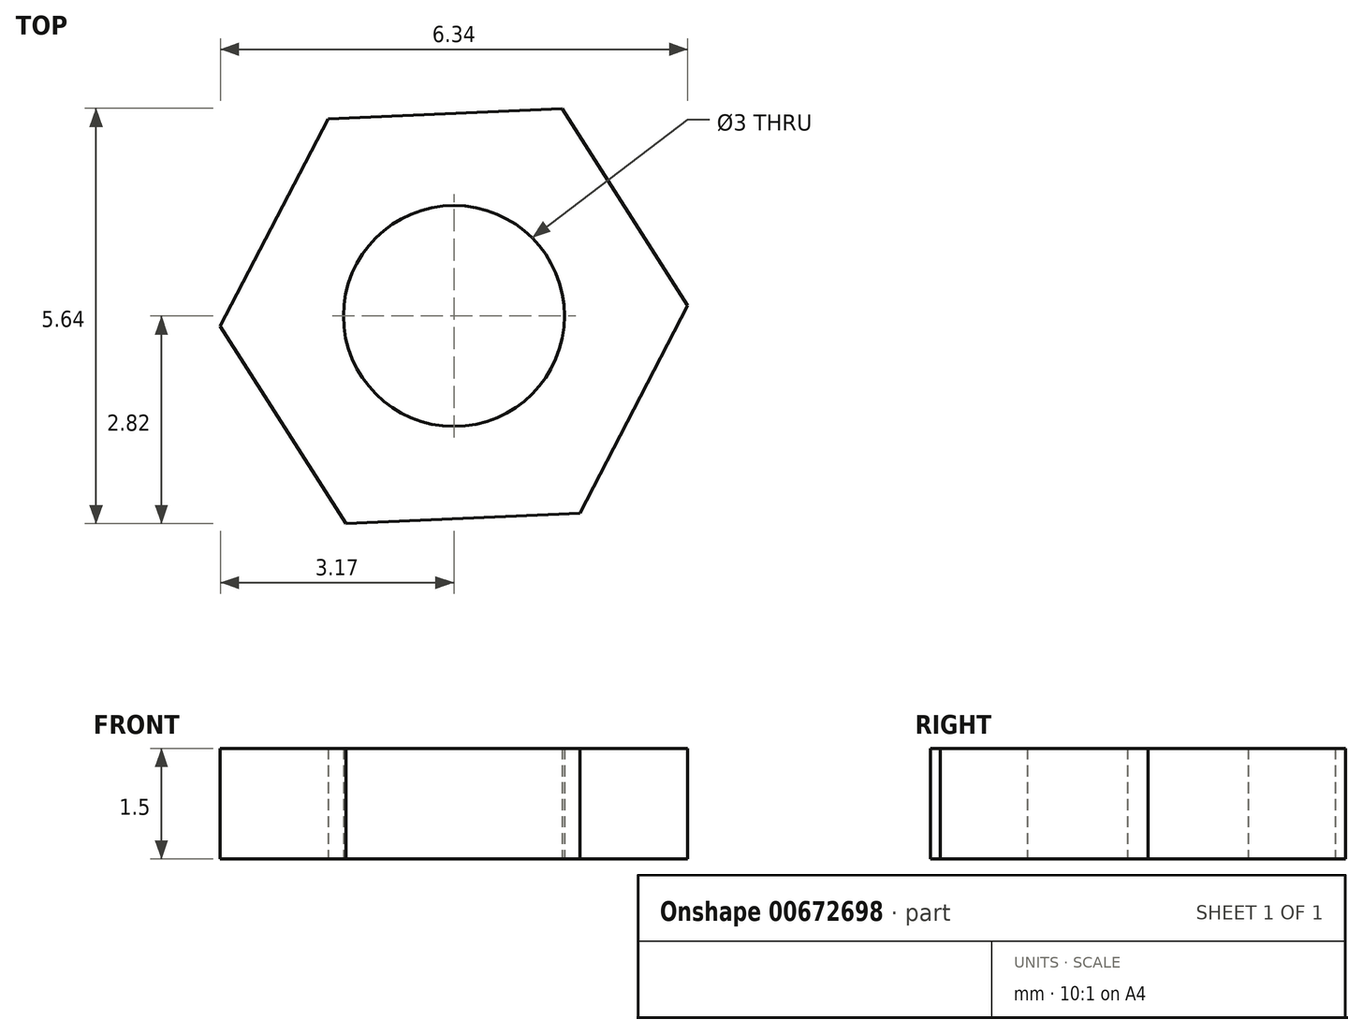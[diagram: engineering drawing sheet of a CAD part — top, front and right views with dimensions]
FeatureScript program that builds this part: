
annotation { "Feature Type Name" : "Feature", "Feature Type Description" : "" }
export const myFeature = defineFeature(function(context is Context, id is Id, definition is map)
    precondition{}
    {
        {
            var Q0;
            Q0=qCreatedBy(makeId("Top.planeOp"),FACE);
            var sketch = newSketch(context, id + "F0", { "sketchPlane" : qUnion([Q0])});
            skCircle(sketch, "E0.cCircle", {"center": v(0, 0) * mm, "radius": 2.75 * mm});
            skLineSegment(sketch, "E0.0", {"start": v(3.17, 0.14) * mm, "end": v(1.7, -2.68) * mm});
            skLineSegment(sketch, "E0.1", {"start": v(1.7, -2.68) * mm, "end": v(-1.47, -2.82) * mm});
            skLineSegment(sketch, "E0.2", {"start": v(-1.47, -2.82) * mm, "end": v(-3.17, -0.14) * mm});
            skLineSegment(sketch, "E0.3", {"start": v(-3.17, -0.14) * mm, "end": v(-1.7, 2.68) * mm});
            skLineSegment(sketch, "E0.4", {"start": v(-1.7, 2.68) * mm, "end": v(1.47, 2.82) * mm});
            skLineSegment(sketch, "E0.5", {"start": v(1.47, 2.82) * mm, "end": v(3.17, 0.14) * mm});
            skPoint(sketch, "E0.0.midPoint", {"position": v(2.44, -1.27) * mm});
            skCircle(sketch, "E1", {"center": v(0, 0) * mm, "radius": 1.5 * mm});
            skPoint(sketch, "E2", {"position": v(-1.47, -2.82) * mm});
            skPoint(sketch, "E3", {"position": v(1.7, -2.68) * mm});
            skSolve(sketch);
        }
        {
            var Q0;
            {var subQ0=sQuery(id+"F0.wireOp",EDGE,"E0.4");var subQ1=sQuery(id+"F0.wireOp",EDGE,"E0.cCircle");var subQ2=makeQuery(id+"F0.imprint","INTERSECT",VERTEX,{"derivedFrom":[subQ1,subQ0]});Q0=makeQuery(id+"F0.imprint","IMPRINT",FACE,{"disambiguationData":[TD([[makeQuery(id+"F0.imprint","IMPRINT",EDGE,{"disambiguationData":[TD([[subQ2,1.0]])],"derivedFrom":subQ1}),-1.0]])]});}
            var Q1;
            {var subQ0=sQuery(id+"F0.wireOp",EDGE,"E0.1");var subQ1=sQuery(id+"F0.wireOp",EDGE,"E0.cCircle");var subQ2=makeQuery(id+"F0.imprint","INTERSECT",VERTEX,{"derivedFrom":[subQ1,subQ0]});Q1=makeQuery(id+"F0.imprint","IMPRINT",FACE,{"disambiguationData":[TD([[makeQuery(id+"F0.imprint","IMPRINT",EDGE,{"disambiguationData":[TD([[subQ2,-1.0]])],"derivedFrom":subQ1}),-1.0]])]});}
            var Q2;
            {var subQ0=sQuery(id+"F0.wireOp",EDGE,"E0.4");var subQ1=sQuery(id+"F0.wireOp",EDGE,"E0.cCircle");var subQ2=makeQuery(id+"F0.imprint","INTERSECT",VERTEX,{"derivedFrom":[subQ1,subQ0]});Q2=makeQuery(id+"F0.imprint","IMPRINT",FACE,{"disambiguationData":[TD([[makeQuery(id+"F0.imprint","IMPRINT",EDGE,{"disambiguationData":[TD([[subQ2,-1.0]])],"derivedFrom":subQ1}),-1.0]])]});}
            var Q3;
            {var subQ0=sQuery(id+"F0.wireOp",EDGE,"E0.5");var subQ1=sQuery(id+"F0.wireOp",EDGE,"E0.cCircle");var subQ2=makeQuery(id+"F0.imprint","INTERSECT",VERTEX,{"derivedFrom":[subQ1,subQ0]});Q3=makeQuery(id+"F0.imprint","IMPRINT",FACE,{"disambiguationData":[TD([[makeQuery(id+"F0.imprint","IMPRINT",EDGE,{"disambiguationData":[TD([[subQ2,1.0]])],"derivedFrom":subQ1}),-1.0]])]});}
            var Q4;
            {var subQ0=sQuery(id+"F0.wireOp",EDGE,"E0.2");var subQ1=sQuery(id+"F0.wireOp",EDGE,"E0.cCircle");var subQ2=makeQuery(id+"F0.imprint","INTERSECT",VERTEX,{"derivedFrom":[subQ1,subQ0]});Q4=makeQuery(id+"F0.imprint","IMPRINT",FACE,{"disambiguationData":[TD([[makeQuery(id+"F0.imprint","IMPRINT",EDGE,{"disambiguationData":[TD([[subQ2,-1.0]])],"derivedFrom":subQ1}),-1.0]])]});}
            var Q5;
            {var subQ0=sQuery(id+"F0.wireOp",EDGE,"E0.3");var subQ1=sQuery(id+"F0.wireOp",EDGE,"E0.cCircle");var subQ2=makeQuery(id+"F0.imprint","INTERSECT",VERTEX,{"derivedFrom":[subQ1,subQ0]});Q5=makeQuery(id+"F0.imprint","IMPRINT",FACE,{"disambiguationData":[TD([[makeQuery(id+"F0.imprint","IMPRINT",EDGE,{"disambiguationData":[TD([[subQ2,-1.0]])],"derivedFrom":subQ1}),-1.0]])]});}
            var Q6;
            Q6=makeQuery(id+"F0.imprint","IMPRINT",FACE,{"disambiguationData":[TD([[makeQuery(id+"F0.imprint","IMPRINT",EDGE,{"derivedFrom":sQuery(id+"F0.wireOp",EDGE,"E1")}),-1.0]])]});
            extrude(context, id + "F1", {"entities" : qUnion([Q0, Q1, Q2, Q3, Q4, Q5, Q6]), "depth" : 1.5 * mm, "offsetDistance" : 25 * mm});
        }
    });
